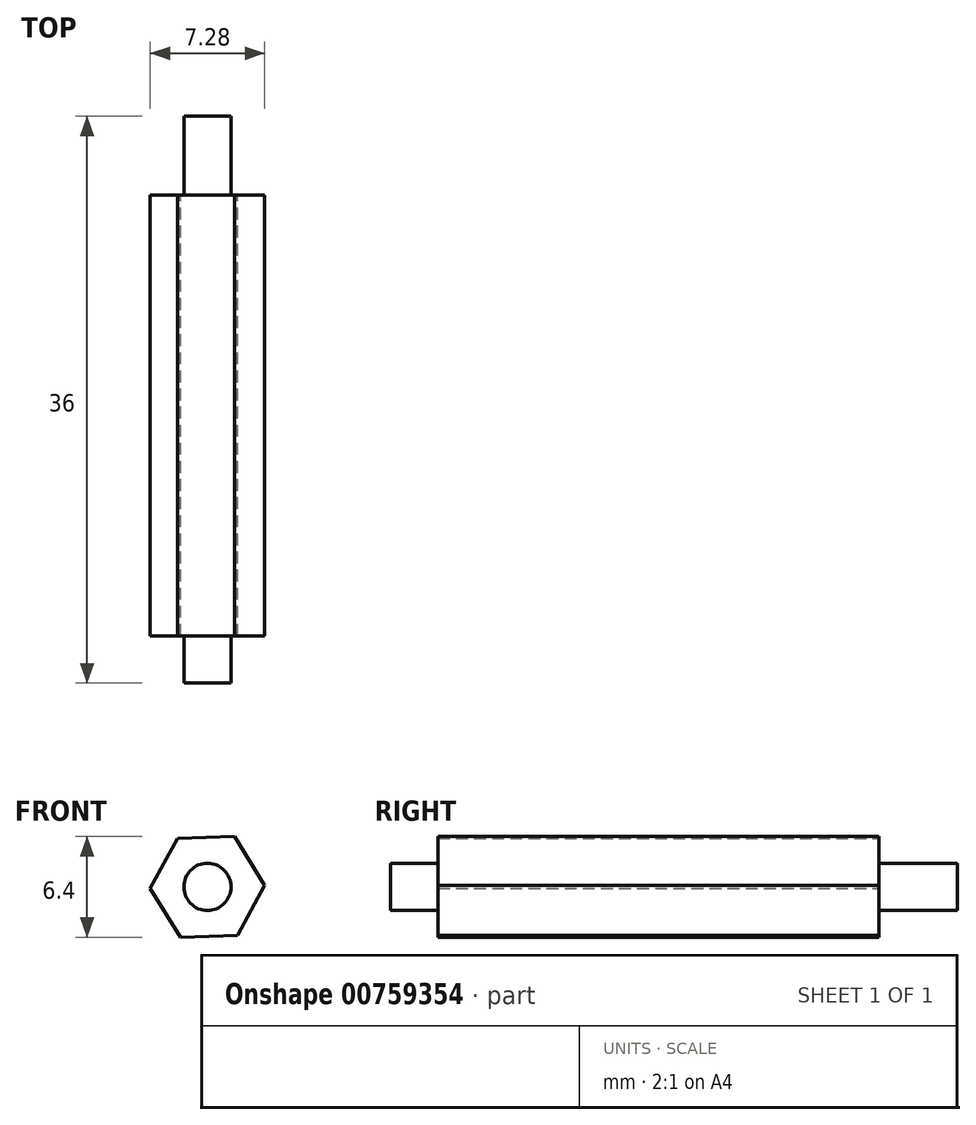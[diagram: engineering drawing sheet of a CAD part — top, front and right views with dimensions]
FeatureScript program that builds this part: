
annotation { "Feature Type Name" : "Feature", "Feature Type Description" : "" }
export const myFeature = defineFeature(function(context is Context, id is Id, definition is map)
    precondition{}
    {
        {
            var Q0;
            Q0=qCreatedBy(makeId("Front.planeOp"),FACE);
            var sketch = newSketch(context, id + "F0", { "sketchPlane" : qUnion([Q0])});
            skCircle(sketch, "E0.cCircle", {"center": v(0, 0) * mm, "radius": 3.15 * mm, "construction": true});
            skLineSegment(sketch, "E0.0", {"start": v(1.72, 3.2) * mm, "end": v(3.64, 0.1) * mm});
            skLineSegment(sketch, "E0.1", {"start": v(3.64, 0.1) * mm, "end": v(1.91, -3.1) * mm});
            skLineSegment(sketch, "E0.2", {"start": v(1.91, -3.1) * mm, "end": v(-1.72, -3.2) * mm});
            skLineSegment(sketch, "E0.3", {"start": v(-1.72, -3.2) * mm, "end": v(-3.64, -0.1) * mm});
            skLineSegment(sketch, "E0.4", {"start": v(-3.64, -0.1) * mm, "end": v(-1.91, 3.1) * mm});
            skLineSegment(sketch, "E0.5", {"start": v(-1.91, 3.1) * mm, "end": v(1.72, 3.2) * mm});
            skPoint(sketch, "E0.0.midPoint", {"position": v(2.68, 1.66) * mm});
            skSolve(sketch);
        }
        {
            var Q0;
            Q0=makeQuery(id+"F0.imprint","IMPRINT",FACE,{"disambiguationData":[TD([[makeQuery(id+"F0.imprint","IMPRINT",EDGE,{"derivedFrom":sQuery(id+"F0.wireOp",EDGE,"E0.0")}),-1.0]])]});
            extrude(context, id + "F1", {"entities" : qUnion([Q0]), "depth" : 28 * mm, "offsetDistance" : 25 * mm});
        }
        {
            var Q0;
            Q0=makeQuery(id+"F1.opExtrude","CAP_FACE",FACE,{"disambiguationData":[OSD([sQuery(id+"F0.wireOp",EDGE,"E0.0"),sQuery(id+"F0.wireOp",EDGE,"E0.1"),sQuery(id+"F0.wireOp",EDGE,"E0.2"),sQuery(id+"F0.wireOp",EDGE,"E0.3"),sQuery(id+"F0.wireOp",EDGE,"E0.4"),sQuery(id+"F0.wireOp",EDGE,"E0.5")])],"isStart":false});
            var sketch = newSketch(context, id + "F2", { "sketchPlane" : qUnion([Q0])});
            skCircle(sketch, "E1", {"center": v(0, 0) * mm, "radius": 1.5 * mm});
            skSolve(sketch);
        }
        {
            var Q0;
            Q0 = qSketchRegion(id + "F2", true);
            extrude(context, id + "F3", {"entities" : qUnion([Q0]), "operationType" : NewBodyOperationType.ADD, "depth" : 3 * mm, "offsetDistance" : 25 * mm});
        }
        {
            var Q0;
            Q0=makeQuery(id+"F1.opExtrude","CAP_FACE",FACE,{"disambiguationData":[OSD([sQuery(id+"F0.wireOp",EDGE,"E0.0"),sQuery(id+"F0.wireOp",EDGE,"E0.1"),sQuery(id+"F0.wireOp",EDGE,"E0.2"),sQuery(id+"F0.wireOp",EDGE,"E0.3"),sQuery(id+"F0.wireOp",EDGE,"E0.4"),sQuery(id+"F0.wireOp",EDGE,"E0.5")])],"isStart":true});
            var sketch = newSketch(context, id + "F4", { "sketchPlane" : qUnion([Q0])});
            skCircle(sketch, "E2", {"center": v(0, 0) * mm, "radius": 1.5 * mm});
            skSolve(sketch);
        }
        {
            var Q0;
            Q0=makeQuery(id+"F4.imprint","IMPRINT",FACE,{"disambiguationData":[TD([[makeQuery(id+"F4.imprint","IMPRINT",EDGE,{"derivedFrom":sQuery(id+"F4.wireOp",EDGE,"E2")}),1.0]])]});
            extrude(context, id + "F5", {"entities" : qUnion([Q0]), "operationType" : NewBodyOperationType.ADD, "depth" : 5 * mm, "offsetDistance" : 25 * mm});
        }
    });
